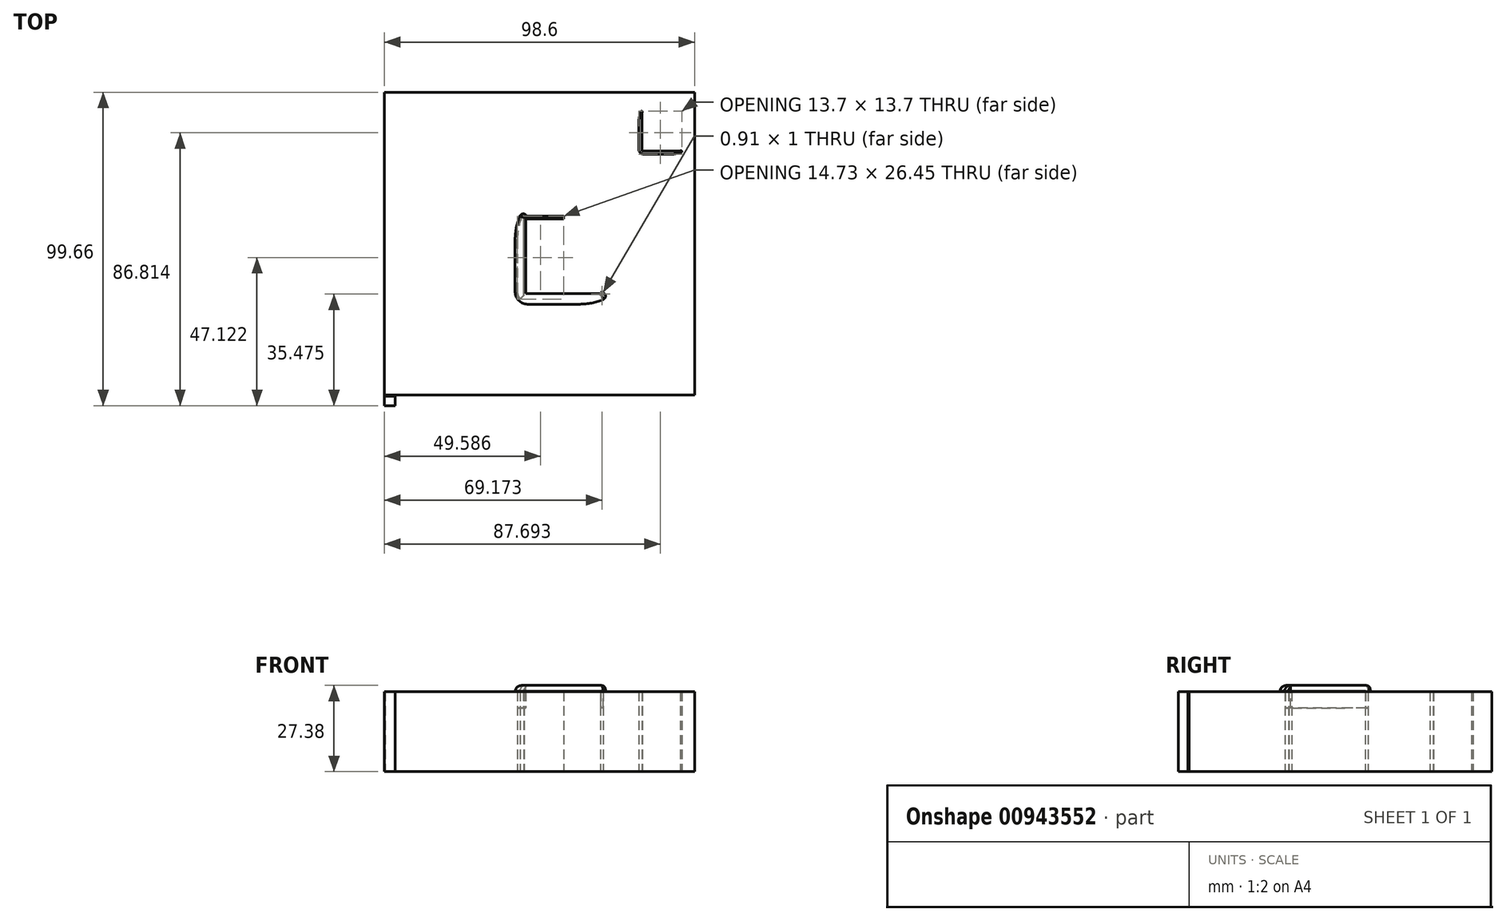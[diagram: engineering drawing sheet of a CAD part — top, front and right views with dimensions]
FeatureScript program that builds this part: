
annotation { "Feature Type Name" : "Feature", "Feature Type Description" : "" }
export const myFeature = defineFeature(function(context is Context, id is Id, definition is map)
    precondition{}
    {
        {
            var Q0;
            Q0=qCreatedBy(makeId("Top.planeOp"),FACE);
            var sketch = newSketch(context, id + "F0", { "sketchPlane" : qUnion([Q0])});
            skLineSegment(sketch, "E0", {"start": v(-49.3, -64.38) * mm, "end": v(49.3, -64.38) * mm});
            skLineSegment(sketch, "E1", {"start": v(49.3, -64.38) * mm, "end": v(49.3, 64.38) * mm});
            skLineSegment(sketch, "E2", {"start": v(49.3, 64.38) * mm, "end": v(-49.3, 64.38) * mm});
            skLineSegment(sketch, "E3", {"start": v(-49.3, 64.38) * mm, "end": v(-49.3, -64.38) * mm});
            skLineSegment(sketch, "E4", {"start": v(-49.3, 60.15) * mm, "end": v(49.3, 60.15) * mm});
            skLineSegment(sketch, "E5", {"start": v(49.3, 60.15) * mm, "end": v(49.3, 59.97) * mm});
            skLineSegment(sketch, "E6", {"start": v(49.3, 59.97) * mm, "end": v(-49.3, 59.97) * mm});
            skLineSegment(sketch, "E7", {"start": v(-49.3, 59.97) * mm, "end": v(-49.3, 60.15) * mm});
            skLineSegment(sketch, "E8", {"start": v(15.26, 64.38) * mm, "end": v(15.43, 64.38) * mm});
            skLineSegment(sketch, "E9", {"start": v(15.43, 64.38) * mm, "end": v(15.43, 59.97) * mm});
            skLineSegment(sketch, "E10", {"start": v(15.43, 59.97) * mm, "end": v(15.26, 59.97) * mm});
            skLineSegment(sketch, "E11", {"start": v(15.26, 59.97) * mm, "end": v(15.26, 64.38) * mm});
            skLineSegment(sketch, "E12", {"start": v(-49.12, -36.34) * mm, "end": v(49.3, -36.34) * mm});
            skLineSegment(sketch, "E13", {"start": v(49.3, -36.34) * mm, "end": v(49.3, -36.69) * mm});
            skLineSegment(sketch, "E14", {"start": v(49.3, -36.69) * mm, "end": v(-49.12, -36.69) * mm});
            skLineSegment(sketch, "E15", {"start": v(-49.12, -36.69) * mm, "end": v(-49.12, -36.34) * mm});
            skLineSegment(sketch, "E16", {"start": v(-6.44, -36.51) * mm, "end": v(-6.09, -36.51) * mm});
            skLineSegment(sketch, "E17", {"start": v(-6.09, -36.51) * mm, "end": v(-6.09, -64.2) * mm});
            skLineSegment(sketch, "E18", {"start": v(-6.09, -64.2) * mm, "end": v(-6.44, -64.2) * mm});
            skLineSegment(sketch, "E19", {"start": v(-6.44, -64.2) * mm, "end": v(-6.44, -36.51) * mm});
            skLineSegment(sketch, "E20", {"start": v(-6.44, -45.33) * mm, "end": v(49.12, -45.33) * mm});
            skLineSegment(sketch, "E21", {"start": v(49.12, -45.33) * mm, "end": v(49.12, -45.68) * mm});
            skLineSegment(sketch, "E22", {"start": v(49.12, -45.68) * mm, "end": v(-6.44, -45.68) * mm});
            skLineSegment(sketch, "E23", {"start": v(-6.44, -45.68) * mm, "end": v(-6.44, -45.33) * mm});
            skLineSegment(sketch, "E24", {"start": v(-6.44, -49.04) * mm, "end": v(49.12, -49.04) * mm});
            skLineSegment(sketch, "E25", {"start": v(49.12, -49.04) * mm, "end": v(49.12, -49.39) * mm});
            skLineSegment(sketch, "E26", {"start": v(49.12, -49.39) * mm, "end": v(-6.44, -49.39) * mm});
            skLineSegment(sketch, "E27", {"start": v(-6.44, -49.39) * mm, "end": v(-6.44, -49.04) * mm});
            skLineSegment(sketch, "E28", {"start": v(-6.09, -52.92) * mm, "end": v(49.3, -52.92) * mm});
            skLineSegment(sketch, "E29", {"start": v(49.3, -52.92) * mm, "end": v(49.3, -53.1) * mm});
            skLineSegment(sketch, "E30", {"start": v(49.3, -53.1) * mm, "end": v(-6.09, -53.1) * mm});
            skLineSegment(sketch, "E31", {"start": v(-6.09, -53.1) * mm, "end": v(-6.09, -52.92) * mm});
            skLineSegment(sketch, "E32", {"start": v(-6.09, -56.62) * mm, "end": v(49.3, -56.62) * mm});
            skLineSegment(sketch, "E33", {"start": v(49.3, -56.62) * mm, "end": v(49.3, -56.8) * mm});
            skLineSegment(sketch, "E34", {"start": v(49.3, -56.8) * mm, "end": v(-6.09, -56.8) * mm});
            skLineSegment(sketch, "E35", {"start": v(-6.09, -56.8) * mm, "end": v(-6.09, -56.62) * mm});
            skLineSegment(sketch, "E36", {"start": v(-6.09, -60.32) * mm, "end": v(49.3, -60.32) * mm});
            skLineSegment(sketch, "E37", {"start": v(49.3, -60.32) * mm, "end": v(49.3, -60.5) * mm});
            skLineSegment(sketch, "E38", {"start": v(49.3, -60.5) * mm, "end": v(-6.09, -60.5) * mm});
            skLineSegment(sketch, "E39", {"start": v(-6.09, -60.5) * mm, "end": v(-6.09, -60.32) * mm});
            skLineSegment(sketch, "E40", {"start": v(21.25, -49.04) * mm, "end": v(21.6, -49.04) * mm});
            skLineSegment(sketch, "E41", {"start": v(21.6, -49.04) * mm, "end": v(21.6, -64.2) * mm});
            skLineSegment(sketch, "E42", {"start": v(21.6, -64.2) * mm, "end": v(21.25, -64.2) * mm});
            skLineSegment(sketch, "E43", {"start": v(21.25, -64.2) * mm, "end": v(21.25, -49.04) * mm});
            skLineSegment(sketch, "E44", {"start": v(-49.3, -47.8) * mm, "end": v(-6.09, -47.8) * mm});
            skLineSegment(sketch, "E45", {"start": v(-6.09, -47.8) * mm, "end": v(-6.09, -48.15) * mm});
            skLineSegment(sketch, "E46", {"start": v(-6.09, -48.15) * mm, "end": v(-49.3, -48.15) * mm});
            skLineSegment(sketch, "E47", {"start": v(-49.3, -48.15) * mm, "end": v(-49.3, -47.8) * mm});
            skLineSegment(sketch, "E48", {"start": v(-49.3, -53.8) * mm, "end": v(-6.09, -53.8) * mm});
            skLineSegment(sketch, "E49", {"start": v(-6.09, -53.8) * mm, "end": v(-6.09, -50.98) * mm});
            skLineSegment(sketch, "E50", {"start": v(-6.09, -50.98) * mm, "end": v(-49.3, -50.98) * mm});
            skLineSegment(sketch, "E51", {"start": v(-49.3, -50.98) * mm, "end": v(-49.3, -53.8) * mm});
            skLineSegment(sketch, "E52", {"start": v(-49.3, -59.09) * mm, "end": v(-6.09, -59.09) * mm});
            skLineSegment(sketch, "E53", {"start": v(-6.09, -59.09) * mm, "end": v(-6.09, -56.27) * mm});
            skLineSegment(sketch, "E54", {"start": v(-6.09, -56.27) * mm, "end": v(-49.3, -56.27) * mm});
            skLineSegment(sketch, "E55", {"start": v(-49.3, -56.27) * mm, "end": v(-49.3, -59.09) * mm});
            skLineSegment(sketch, "E56", {"start": v(-49.3, -64.38) * mm, "end": v(-6.09, -64.38) * mm});
            skLineSegment(sketch, "E57", {"start": v(-6.09, -64.38) * mm, "end": v(-6.09, -61.56) * mm});
            skLineSegment(sketch, "E58", {"start": v(-6.09, -61.56) * mm, "end": v(-49.3, -61.56) * mm});
            skLineSegment(sketch, "E59", {"start": v(-49.3, -61.56) * mm, "end": v(-49.3, -64.38) * mm});
            skLineSegment(sketch, "E60", {"start": v(-49.3, -48.15) * mm, "end": v(-6.09, -48.15) * mm});
            skLineSegment(sketch, "E61", {"start": v(-6.09, -48.15) * mm, "end": v(-6.09, -45.33) * mm});
            skLineSegment(sketch, "E62", {"start": v(-6.09, -45.33) * mm, "end": v(-49.3, -45.33) * mm});
            skLineSegment(sketch, "E63", {"start": v(-49.3, -45.33) * mm, "end": v(-49.3, -48.15) * mm});
            skLineSegment(sketch, "E64", {"start": v(-49.3, -42.5) * mm, "end": v(-6.09, -42.5) * mm});
            skLineSegment(sketch, "E65", {"start": v(-6.09, -42.5) * mm, "end": v(-6.09, -39.69) * mm});
            skLineSegment(sketch, "E66", {"start": v(-6.09, -39.69) * mm, "end": v(-49.3, -39.69) * mm});
            skLineSegment(sketch, "E67", {"start": v(-49.3, -39.69) * mm, "end": v(-49.3, -42.5) * mm});
            skArc(sketch, "E68", {"start": v(-46.48, -62.8) * mm, "mid": v(-46.5, -62.62) * mm, "end": v(-46.54, -62.46) * mm});
            skArc(sketch, "E69", {"start": v(-46.54, -62.46) * mm, "mid": v(-46.63, -62.3) * mm, "end": v(-46.74, -62.17) * mm});
            skArc(sketch, "E70", {"start": v(-46.74, -62.17) * mm, "mid": v(-46.87, -62.06) * mm, "end": v(-47.02, -61.98) * mm});
            skArc(sketch, "E71", {"start": v(-47.02, -61.98) * mm, "mid": v(-47.19, -61.93) * mm, "end": v(-47.36, -61.91) * mm});
            skArc(sketch, "E72", {"start": v(-47.36, -61.91) * mm, "mid": v(-47.53, -61.93) * mm, "end": v(-47.7, -61.98) * mm});
            skArc(sketch, "E73", {"start": v(-47.7, -61.98) * mm, "mid": v(-47.85, -62.06) * mm, "end": v(-47.98, -62.17) * mm});
            skArc(sketch, "E74", {"start": v(-47.98, -62.17) * mm, "mid": v(-48.1, -62.3) * mm, "end": v(-48.17, -62.46) * mm});
            skArc(sketch, "E75", {"start": v(-48.17, -62.46) * mm, "mid": v(-48.22, -62.62) * mm, "end": v(-48.24, -62.8) * mm});
            skArc(sketch, "E76", {"start": v(-48.24, -62.8) * mm, "mid": v(-48.22, -62.97) * mm, "end": v(-48.17, -63.13) * mm});
            skArc(sketch, "E77", {"start": v(-48.17, -63.13) * mm, "mid": v(-48.1, -63.28) * mm, "end": v(-47.98, -63.42) * mm});
            skArc(sketch, "E78", {"start": v(-47.98, -63.42) * mm, "mid": v(-47.85, -63.53) * mm, "end": v(-47.7, -63.6) * mm});
            skArc(sketch, "E79", {"start": v(-47.7, -63.6) * mm, "mid": v(-47.53, -63.66) * mm, "end": v(-47.36, -63.68) * mm});
            skArc(sketch, "E80", {"start": v(-47.36, -63.68) * mm, "mid": v(-47.19, -63.66) * mm, "end": v(-47.02, -63.6) * mm});
            skArc(sketch, "E81", {"start": v(-47.02, -63.6) * mm, "mid": v(-46.87, -63.53) * mm, "end": v(-46.74, -63.42) * mm});
            skArc(sketch, "E82", {"start": v(-46.74, -63.42) * mm, "mid": v(-46.63, -63.28) * mm, "end": v(-46.54, -63.13) * mm});
            skArc(sketch, "E83", {"start": v(-46.54, -63.13) * mm, "mid": v(-46.5, -62.97) * mm, "end": v(-46.48, -62.8) * mm});
            skArc(sketch, "E84", {"start": v(-38.01, -62.8) * mm, "mid": v(-38.03, -62.62) * mm, "end": v(-38.08, -62.46) * mm});
            skArc(sketch, "E85", {"start": v(-38.08, -62.46) * mm, "mid": v(-38.16, -62.3) * mm, "end": v(-38.27, -62.17) * mm});
            skArc(sketch, "E86", {"start": v(-38.27, -62.17) * mm, "mid": v(-38.4, -62.06) * mm, "end": v(-38.56, -61.98) * mm});
            skArc(sketch, "E87", {"start": v(-38.56, -61.98) * mm, "mid": v(-38.72, -61.93) * mm, "end": v(-38.9, -61.91) * mm});
            skArc(sketch, "E88", {"start": v(-38.9, -61.91) * mm, "mid": v(-39.07, -61.93) * mm, "end": v(-39.23, -61.98) * mm});
            skArc(sketch, "E89", {"start": v(-39.23, -61.98) * mm, "mid": v(-39.38, -62.06) * mm, "end": v(-39.52, -62.17) * mm});
            skArc(sketch, "E90", {"start": v(-39.52, -62.17) * mm, "mid": v(-39.63, -62.3) * mm, "end": v(-39.7, -62.46) * mm});
            skArc(sketch, "E91", {"start": v(-39.7, -62.46) * mm, "mid": v(-39.76, -62.62) * mm, "end": v(-39.78, -62.8) * mm});
            skArc(sketch, "E92", {"start": v(-39.78, -62.8) * mm, "mid": v(-39.76, -62.97) * mm, "end": v(-39.7, -63.13) * mm});
            skArc(sketch, "E93", {"start": v(-39.7, -63.13) * mm, "mid": v(-39.63, -63.28) * mm, "end": v(-39.52, -63.42) * mm});
            skArc(sketch, "E94", {"start": v(-39.52, -63.42) * mm, "mid": v(-39.38, -63.53) * mm, "end": v(-39.23, -63.6) * mm});
            skArc(sketch, "E95", {"start": v(-39.23, -63.6) * mm, "mid": v(-39.07, -63.66) * mm, "end": v(-38.9, -63.68) * mm});
            skArc(sketch, "E96", {"start": v(-38.9, -63.68) * mm, "mid": v(-38.72, -63.66) * mm, "end": v(-38.56, -63.6) * mm});
            skArc(sketch, "E97", {"start": v(-38.56, -63.6) * mm, "mid": v(-38.4, -63.53) * mm, "end": v(-38.27, -63.42) * mm});
            skArc(sketch, "E98", {"start": v(-38.27, -63.42) * mm, "mid": v(-38.16, -63.28) * mm, "end": v(-38.08, -63.13) * mm});
            skArc(sketch, "E99", {"start": v(-38.08, -63.13) * mm, "mid": v(-38.03, -62.97) * mm, "end": v(-38.01, -62.8) * mm});
            skArc(sketch, "E100", {"start": v(-23.55, -62.8) * mm, "mid": v(-23.56, -62.62) * mm, "end": v(-23.62, -62.46) * mm});
            skArc(sketch, "E101", {"start": v(-23.62, -62.46) * mm, "mid": v(-23.7, -62.3) * mm, "end": v(-23.8, -62.17) * mm});
            skArc(sketch, "E102", {"start": v(-23.8, -62.17) * mm, "mid": v(-23.94, -62.06) * mm, "end": v(-24.1, -61.98) * mm});
            skArc(sketch, "E103", {"start": v(-24.1, -61.98) * mm, "mid": v(-24.26, -61.93) * mm, "end": v(-24.43, -61.91) * mm});
            skArc(sketch, "E104", {"start": v(-24.43, -61.91) * mm, "mid": v(-24.6, -61.93) * mm, "end": v(-24.77, -61.98) * mm});
            skArc(sketch, "E105", {"start": v(-24.77, -61.98) * mm, "mid": v(-24.92, -62.06) * mm, "end": v(-25.05, -62.17) * mm});
            skArc(sketch, "E106", {"start": v(-25.05, -62.17) * mm, "mid": v(-25.16, -62.3) * mm, "end": v(-25.24, -62.46) * mm});
            skArc(sketch, "E107", {"start": v(-25.24, -62.46) * mm, "mid": v(-25.3, -62.62) * mm, "end": v(-25.31, -62.8) * mm});
            skArc(sketch, "E108", {"start": v(-25.31, -62.8) * mm, "mid": v(-25.3, -62.97) * mm, "end": v(-25.24, -63.13) * mm});
            skArc(sketch, "E109", {"start": v(-25.24, -63.13) * mm, "mid": v(-25.16, -63.28) * mm, "end": v(-25.05, -63.42) * mm});
            skArc(sketch, "E110", {"start": v(-25.05, -63.42) * mm, "mid": v(-24.92, -63.53) * mm, "end": v(-24.77, -63.6) * mm});
            skArc(sketch, "E111", {"start": v(-24.77, -63.6) * mm, "mid": v(-24.6, -63.66) * mm, "end": v(-24.43, -63.68) * mm});
            skArc(sketch, "E112", {"start": v(-24.43, -63.68) * mm, "mid": v(-24.26, -63.66) * mm, "end": v(-24.1, -63.6) * mm});
            skArc(sketch, "E113", {"start": v(-24.1, -63.6) * mm, "mid": v(-23.94, -63.53) * mm, "end": v(-23.8, -63.42) * mm});
            skArc(sketch, "E114", {"start": v(-23.8, -63.42) * mm, "mid": v(-23.7, -63.28) * mm, "end": v(-23.62, -63.13) * mm});
            skArc(sketch, "E115", {"start": v(-23.62, -63.13) * mm, "mid": v(-23.56, -62.97) * mm, "end": v(-23.55, -62.8) * mm});
            skLineSegment(sketch, "E116", {"start": v(-4.68, -39.46) * mm, "end": v(-4.68, -39.2) * mm});
            skLineSegment(sketch, "E117", {"start": v(-4.68, -39.2) * mm, "end": v(-2.48, -39.2) * mm});
            skLineSegment(sketch, "E118", {"start": v(-2.48, -39.2) * mm, "end": v(-2.48, -38.95) * mm});
            skLineSegment(sketch, "E119", {"start": v(-2.48, -38.95) * mm, "end": v(-4.68, -38.95) * mm});
            skLineSegment(sketch, "E120", {"start": v(-4.68, -38.95) * mm, "end": v(-4.68, -37.29) * mm});
            skLineSegment(sketch, "E121", {"start": v(-4.68, -37.29) * mm, "end": v(-1.9, -37.29) * mm});
            skArc(sketch, "E122", {"start": v(-1.9, -37.3) * mm, "mid": v(-1.01, -37.67) * mm, "end": v(-0.64, -38.57) * mm});
            skArc(sketch, "E123", {"start": v(-0.64, -38.57) * mm, "mid": v(-1.01, -39.46) * mm, "end": v(-1.9, -39.84) * mm});
            skLineSegment(sketch, "E124", {"start": v(-1.9, -39.84) * mm, "end": v(-2.48, -39.84) * mm});
            skLineSegment(sketch, "E125", {"start": v(-2.48, -39.84) * mm, "end": v(-2.48, -39.97) * mm});
            skLineSegment(sketch, "E126", {"start": v(-2.48, -39.97) * mm, "end": v(-4.68, -39.97) * mm});
            skLineSegment(sketch, "E127", {"start": v(-4.68, -39.97) * mm, "end": v(-4.68, -39.72) * mm});
            skLineSegment(sketch, "E128", {"start": v(-4.68, -39.72) * mm, "end": v(-2.48, -39.72) * mm});
            skLineSegment(sketch, "E129", {"start": v(-2.48, -39.72) * mm, "end": v(-2.48, -39.46) * mm});
            skLineSegment(sketch, "E130", {"start": v(-2.48, -39.46) * mm, "end": v(-4.68, -39.46) * mm});
            skLineSegment(sketch, "E131", {"start": v(-2.48, -40.23) * mm, "end": v(-4.68, -40.23) * mm});
            skLineSegment(sketch, "E132", {"start": v(-2.48, -40.48) * mm, "end": v(-4.68, -40.48) * mm});
            skLineSegment(sketch, "E133", {"start": v(-4.68, -40.48) * mm, "end": v(-4.68, -40.23) * mm});
            skLineSegment(sketch, "E134", {"start": v(-2.48, -40.23) * mm, "end": v(-2.48, -40.48) * mm});
            skLineSegment(sketch, "E135", {"start": v(2.09, -38.5) * mm, "end": v(3.79, -39.27) * mm});
            skLineSegment(sketch, "E136", {"start": v(2.53, -39.59) * mm, "end": v(1.84, -39.59) * mm});
            skLineSegment(sketch, "E137", {"start": v(0.7, -37.29) * mm, "end": v(4.11, -37.29) * mm});
            skLineSegment(sketch, "E138", {"start": v(0.7, -37.29) * mm, "end": v(2.68, -38.18) * mm});
            skLineSegment(sketch, "E139", {"start": v(-0.28, -37.73) * mm, "end": v(3.13, -39.27) * mm});
            skLineSegment(sketch, "E140", {"start": v(2.09, -38.5) * mm, "end": v(2.74, -38.5) * mm});
            skLineSegment(sketch, "E141", {"start": v(4.11, -40.48) * mm, "end": v(-0.28, -40.48) * mm});
            skLineSegment(sketch, "E142", {"start": v(-0.28, -38.32) * mm, "end": v(-0.28, -40.48) * mm});
            skLineSegment(sketch, "E143", {"start": v(1.84, -39.27) * mm, "end": v(1.84, -39.59) * mm});
            skLineSegment(sketch, "E144", {"start": v(-0.28, -37.44) * mm, "end": v(1.84, -38.39) * mm});
            skLineSegment(sketch, "E145", {"start": v(0.05, -37.29) * mm, "end": v(2.03, -38.18) * mm});
            skLineSegment(sketch, "E146", {"start": v(-0.28, -37.73) * mm, "end": v(-0.28, -38.03) * mm});
            skLineSegment(sketch, "E147", {"start": v(-0.28, -37.29) * mm, "end": v(0.05, -37.29) * mm});
            skLineSegment(sketch, "E148", {"start": v(-0.28, -37.29) * mm, "end": v(-0.28, -37.44) * mm});
            skLineSegment(sketch, "E149", {"start": v(1.84, -38.18) * mm, "end": v(1.84, -38.39) * mm});
            skLineSegment(sketch, "E150", {"start": v(1.84, -38.18) * mm, "end": v(2.03, -38.18) * mm});
            skLineSegment(sketch, "E151", {"start": v(3.4, -38.5) * mm, "end": v(4.11, -38.83) * mm});
            skLineSegment(sketch, "E152", {"start": v(2.74, -38.5) * mm, "end": v(4.11, -39.12) * mm});
            skLineSegment(sketch, "E153", {"start": v(4.11, -38.5) * mm, "end": v(4.11, -38.83) * mm});
            skLineSegment(sketch, "E154", {"start": v(3.84, -39.59) * mm, "end": v(4.11, -39.71) * mm});
            skLineSegment(sketch, "E155", {"start": v(2.53, -39.59) * mm, "end": v(4.11, -40.3) * mm});
            skLineSegment(sketch, "E156", {"start": v(3.19, -39.59) * mm, "end": v(4.11, -40) * mm});
            skLineSegment(sketch, "E157", {"start": v(4.11, -39.27) * mm, "end": v(3.79, -39.27) * mm});
            skLineSegment(sketch, "E158", {"start": v(3.13, -39.27) * mm, "end": v(2.48, -39.27) * mm});
            skLineSegment(sketch, "E159", {"start": v(3.84, -39.59) * mm, "end": v(3.19, -39.59) * mm});
            skLineSegment(sketch, "E160", {"start": v(4.11, -40.3) * mm, "end": v(4.11, -40.48) * mm});
            skLineSegment(sketch, "E161", {"start": v(4.11, -39.12) * mm, "end": v(4.11, -39.27) * mm});
            skLineSegment(sketch, "E162", {"start": v(4.11, -39.71) * mm, "end": v(4.11, -40) * mm});
            skLineSegment(sketch, "E163", {"start": v(2.68, -38.18) * mm, "end": v(4.11, -38.18) * mm});
            skLineSegment(sketch, "E164", {"start": v(3.4, -38.5) * mm, "end": v(4.11, -38.5) * mm});
            skLineSegment(sketch, "E165", {"start": v(4.11, -37.29) * mm, "end": v(4.11, -38.18) * mm});
            skLineSegment(sketch, "E166", {"start": v(-0.28, -38.32) * mm, "end": v(-0.28, -38.03) * mm});
            skLineSegment(sketch, "E167", {"start": v(1.84, -39.27) * mm, "end": v(2.48, -39.27) * mm});
            skLineSegment(sketch, "E168", {"start": v(-49.12, -36.34) * mm, "end": v(-45.95, -36.34) * mm});
            skLineSegment(sketch, "E169", {"start": v(-45.95, -36.34) * mm, "end": v(-45.95, -47.8) * mm});
            skLineSegment(sketch, "E170", {"start": v(-2.58, -40.48) * mm, "end": v(-2.48, -40.43) * mm});
            skLineSegment(sketch, "E171", {"start": v(1.97, -37.86) * mm, "end": v(2.95, -37.29) * mm});
            skLineSegment(sketch, "E172", {"start": v(-1.32, -39.76) * mm, "end": v(-0.63, -39.36) * mm});
            skLineSegment(sketch, "E173", {"start": v(1.4, -38.2) * mm, "end": v(1.68, -38.03) * mm});
            skLineSegment(sketch, "E174", {"start": v(-0.28, -39.16) * mm, "end": v(1.1, -38.36) * mm});
            skLineSegment(sketch, "E175", {"start": v(-3.21, -40.48) * mm, "end": v(-2.77, -40.23) * mm});
            skLineSegment(sketch, "E176", {"start": v(1.6, -37.7) * mm, "end": v(2.32, -37.29) * mm});
            skLineSegment(sketch, "E177", {"start": v(-2.1, -39.84) * mm, "end": v(-0.31, -38.8) * mm});
            skLineSegment(sketch, "E178", {"start": v(1.04, -38.03) * mm, "end": v(1.32, -37.86) * mm});
            skLineSegment(sketch, "E179", {"start": v(-0.28, -38.8) * mm, "end": v(0.75, -38.2) * mm});
            skLineSegment(sketch, "E180", {"start": v(-3.85, -40.48) * mm, "end": v(-3.4, -40.23) * mm});
            skLineSegment(sketch, "E181", {"start": v(1.25, -37.54) * mm, "end": v(1.68, -37.29) * mm});
            skLineSegment(sketch, "E182", {"start": v(-2.96, -39.97) * mm, "end": v(-2.52, -39.72) * mm});
            skLineSegment(sketch, "E183", {"start": v(0.68, -37.87) * mm, "end": v(0.97, -37.7) * mm});
            skLineSegment(sketch, "E184", {"start": v(-2.48, -39.7) * mm, "end": v(-0.3, -38.43) * mm});
            skLineSegment(sketch, "E185", {"start": v(-0.28, -38.42) * mm, "end": v(0.4, -38.03) * mm});
            skLineSegment(sketch, "E186", {"start": v(-4.48, -40.48) * mm, "end": v(-4.04, -40.23) * mm});
            skLineSegment(sketch, "E187", {"start": v(0.9, -37.38) * mm, "end": v(1.05, -37.29) * mm});
            skLineSegment(sketch, "E188", {"start": v(-3.6, -39.97) * mm, "end": v(-3.15, -39.72) * mm});
            skLineSegment(sketch, "E189", {"start": v(0.32, -37.7) * mm, "end": v(0.6, -37.54) * mm});
            skLineSegment(sketch, "E190", {"start": v(-2.71, -39.46) * mm, "end": v(-0.39, -38.12) * mm});
            skLineSegment(sketch, "E191", {"start": v(-0.28, -38.06) * mm, "end": v(0.04, -37.87) * mm});
            skLineSegment(sketch, "E192", {"start": v(-4.68, -40.23) * mm, "end": v(-4.67, -40.23) * mm});
            skLineSegment(sketch, "E193", {"start": v(-0.03, -37.55) * mm, "end": v(0.25, -37.38) * mm});
            skLineSegment(sketch, "E194", {"start": v(-4.23, -39.97) * mm, "end": v(-3.79, -39.72) * mm});
            skLineSegment(sketch, "E195", {"start": v(-2.48, -38.96) * mm, "end": v(-0.56, -37.85) * mm});
            skLineSegment(sketch, "E196", {"start": v(-3.35, -39.46) * mm, "end": v(-2.9, -39.2) * mm});
            skLineSegment(sketch, "E197", {"start": v(-4.68, -39.86) * mm, "end": v(-4.42, -39.72) * mm});
            skLineSegment(sketch, "E198", {"start": v(-0.28, -37.32) * mm, "end": v(-0.22, -37.29) * mm});
            skLineSegment(sketch, "E199", {"start": v(-3.98, -39.46) * mm, "end": v(-3.54, -39.2) * mm});
            skLineSegment(sketch, "E200", {"start": v(-3.1, -38.95) * mm, "end": v(-0.8, -37.63) * mm});
            skLineSegment(sketch, "E201", {"start": v(-4.62, -39.46) * mm, "end": v(-4.18, -39.2) * mm});
            skLineSegment(sketch, "E202", {"start": v(-3.73, -38.95) * mm, "end": v(-1.13, -37.45) * mm});
            skLineSegment(sketch, "E203", {"start": v(-4.37, -38.95) * mm, "end": v(-1.55, -37.32) * mm});
            skLineSegment(sketch, "E204", {"start": v(-4.68, -38.76) * mm, "end": v(-2.13, -37.29) * mm});
            skLineSegment(sketch, "E205", {"start": v(-4.68, -38.4) * mm, "end": v(-2.76, -37.29) * mm});
            skLineSegment(sketch, "E206", {"start": v(-4.68, -38.03) * mm, "end": v(-3.4, -37.29) * mm});
            skLineSegment(sketch, "E207", {"start": v(-4.68, -37.66) * mm, "end": v(-4.03, -37.29) * mm});
            skLineSegment(sketch, "E208", {"start": v(-4.68, -37.3) * mm, "end": v(-4.67, -37.29) * mm});
            skLineSegment(sketch, "E209", {"start": v(-0.28, -39.52) * mm, "end": v(1.46, -38.52) * mm});
            skLineSegment(sketch, "E210", {"start": v(2.32, -38.02) * mm, "end": v(3.59, -37.29) * mm});
            skLineSegment(sketch, "E211", {"start": v(1.75, -38.35) * mm, "end": v(1.84, -38.3) * mm});
            skLineSegment(sketch, "E212", {"start": v(-0.28, -39.9) * mm, "end": v(1.82, -38.68) * mm});
            skLineSegment(sketch, "E213", {"start": v(2.68, -38.18) * mm, "end": v(4.11, -37.35) * mm});
            skLineSegment(sketch, "E214", {"start": v(2.1, -38.51) * mm, "end": v(2.12, -38.5) * mm});
            skLineSegment(sketch, "E215", {"start": v(-0.28, -40.26) * mm, "end": v(2.18, -38.84) * mm});
            skLineSegment(sketch, "E216", {"start": v(3.3, -38.18) * mm, "end": v(4.11, -37.72) * mm});
            skLineSegment(sketch, "E217", {"start": v(2.46, -38.67) * mm, "end": v(2.75, -38.5) * mm});
            skLineSegment(sketch, "E218", {"start": v(-0.04, -40.48) * mm, "end": v(1.84, -39.4) * mm});
            skLineSegment(sketch, "E219", {"start": v(3.94, -38.18) * mm, "end": v(4.11, -38.09) * mm});
            skLineSegment(sketch, "E220", {"start": v(2.06, -39.27) * mm, "end": v(2.53, -39) * mm});
            skLineSegment(sketch, "E221", {"start": v(2.82, -38.83) * mm, "end": v(3.1, -38.67) * mm});
            skLineSegment(sketch, "E222", {"start": v(0.6, -40.48) * mm, "end": v(2.15, -39.59) * mm});
            skLineSegment(sketch, "E223", {"start": v(3.75, -38.66) * mm, "end": v(4.03, -38.5) * mm});
            skLineSegment(sketch, "E224", {"start": v(2.7, -39.27) * mm, "end": v(2.89, -39.16) * mm});
            skLineSegment(sketch, "E225", {"start": v(3.18, -39) * mm, "end": v(3.46, -38.83) * mm});
            skLineSegment(sketch, "E226", {"start": v(1.23, -40.48) * mm, "end": v(2.67, -39.65) * mm});
            skLineSegment(sketch, "E227", {"start": v(4.1, -38.82) * mm, "end": v(4.11, -38.82) * mm});
            skLineSegment(sketch, "E228", {"start": v(3.53, -39.15) * mm, "end": v(3.82, -38.99) * mm});
            skLineSegment(sketch, "E229", {"start": v(1.87, -40.48) * mm, "end": v(3.03, -39.81) * mm});
            skLineSegment(sketch, "E230", {"start": v(3.97, -39.27) * mm, "end": v(4.11, -39.19) * mm});
            skLineSegment(sketch, "E231", {"start": v(3.32, -39.65) * mm, "end": v(3.42, -39.59) * mm});
            skLineSegment(sketch, "E232", {"start": v(2.5, -40.48) * mm, "end": v(3.39, -39.97) * mm});
            skLineSegment(sketch, "E233", {"start": v(3.67, -39.8) * mm, "end": v(3.96, -39.64) * mm});
            skLineSegment(sketch, "E234", {"start": v(3.14, -40.48) * mm, "end": v(3.74, -40.13) * mm});
            skLineSegment(sketch, "E235", {"start": v(4.03, -39.97) * mm, "end": v(4.11, -39.92) * mm});
            skLineSegment(sketch, "E236", {"start": v(3.77, -40.48) * mm, "end": v(4.1, -40.3) * mm});
            skLineSegment(sketch, "E237", {"start": v(6.9, 7.22) * mm, "end": v(-11.38, -11.05) * mm});
            skLineSegment(sketch, "E238", {"start": v(44.8, 41.29) * mm, "end": v(32.79, 41.29) * mm});
            skArc(sketch, "E239", {"start": v(32.79, 41.29) * mm, "mid": v(32.7, 41.3) * mm, "end": v(32.62, 41.36) * mm});
            skArc(sketch, "E240", {"start": v(32.62, 41.36) * mm, "mid": v(32.57, 41.43) * mm, "end": v(32.56, 41.52) * mm});
            skLineSegment(sketch, "E241", {"start": v(32.56, 41.52) * mm, "end": v(32.56, 53.52) * mm});
            skArc(sketch, "E242", {"start": v(32.56, 53.52) * mm, "mid": v(32.75, 53.77) * mm, "end": v(32.52, 53.98) * mm});
            skLineSegment(sketch, "E243", {"start": v(32.52, 53.98) * mm, "end": v(32.46, 53.98) * mm});
            skArc(sketch, "E244", {"start": v(32.46, 53.98) * mm, "mid": v(32.33, 53.94) * mm, "end": v(32.24, 53.83) * mm});
            skArc(sketch, "E245", {"start": v(32.24, 53.83) * mm, "mid": v(31.72, 52.07) * mm, "end": v(31.54, 50.24) * mm});
            skLineSegment(sketch, "E246", {"start": v(31.54, 50.24) * mm, "end": v(31.54, 41.9) * mm});
            skArc(sketch, "E247", {"start": v(31.54, 41.9) * mm, "mid": v(31.67, 41.28) * mm, "end": v(32.02, 40.75) * mm});
            skArc(sketch, "E248", {"start": v(32.02, 40.75) * mm, "mid": v(32.55, 40.4) * mm, "end": v(33.17, 40.27) * mm});
            skLineSegment(sketch, "E249", {"start": v(33.17, 40.27) * mm, "end": v(41.51, 40.27) * mm});
            skArc(sketch, "E250", {"start": v(41.51, 40.27) * mm, "mid": v(43.34, 40.45) * mm, "end": v(45.1, 40.98) * mm});
            skArc(sketch, "E251", {"start": v(45.1, 40.98) * mm, "mid": v(45.2, 41.06) * mm, "end": v(45.24, 41.19) * mm});
            skLineSegment(sketch, "E252", {"start": v(45.24, 41.19) * mm, "end": v(45.24, 41.25) * mm});
            skArc(sketch, "E253", {"start": v(45.24, 41.25) * mm, "mid": v(45.03, 41.48) * mm, "end": v(44.8, 41.29) * mm});
            skLineSegment(sketch, "E254", {"start": v(19.42, -4.72) * mm, "end": v(-4.6, -4.72) * mm});
            skArc(sketch, "E255", {"start": v(-4.6, -4.72) * mm, "mid": v(-4.77, -4.68) * mm, "end": v(-4.91, -4.58) * mm});
            skArc(sketch, "E256", {"start": v(-4.91, -4.58) * mm, "mid": v(-5.01, -4.43) * mm, "end": v(-5.05, -4.26) * mm});
            skLineSegment(sketch, "E257", {"start": v(-5.05, -4.26) * mm, "end": v(-5.05, 19.75) * mm});
            skArc(sketch, "E258", {"start": v(-5.05, 19.75) * mm, "mid": v(-4.67, 20.24) * mm, "end": v(-5.12, 20.66) * mm});
            skLineSegment(sketch, "E259", {"start": v(-5.12, 20.66) * mm, "end": v(-5.25, 20.66) * mm});
            skArc(sketch, "E260", {"start": v(-5.25, 20.66) * mm, "mid": v(-5.5, 20.58) * mm, "end": v(-5.67, 20.37) * mm});
            skArc(sketch, "E261", {"start": v(-5.67, 20.37) * mm, "mid": v(-6.73, 16.85) * mm, "end": v(-7.08, 13.2) * mm});
            skLineSegment(sketch, "E262", {"start": v(-7.08, 13.2) * mm, "end": v(-7.08, -3.49) * mm});
            skArc(sketch, "E263", {"start": v(-7.08, -3.49) * mm, "mid": v(-6.83, -4.74) * mm, "end": v(-6.13, -5.8) * mm});
            skArc(sketch, "E264", {"start": v(-6.13, -5.8) * mm, "mid": v(-5.07, -6.5) * mm, "end": v(-3.82, -6.75) * mm});
            skLineSegment(sketch, "E265", {"start": v(-3.82, -6.75) * mm, "end": v(12.86, -6.75) * mm});
            skArc(sketch, "E266", {"start": v(12.86, -6.75) * mm, "mid": v(16.52, -6.4) * mm, "end": v(20.04, -5.34) * mm});
            skArc(sketch, "E267", {"start": v(20.04, -5.34) * mm, "mid": v(20.25, -5.17) * mm, "end": v(20.33, -4.92) * mm});
            skLineSegment(sketch, "E268", {"start": v(20.33, -4.92) * mm, "end": v(20.33, -4.8) * mm});
            skArc(sketch, "E269", {"start": v(20.33, -4.8) * mm, "mid": v(19.9, -4.34) * mm, "end": v(19.42, -4.72) * mm});
            skSolve(sketch);
        }
        {
            var Q0;
            Q0=makeQuery(id+"F0.imprint","IMPRINT",FACE,{"disambiguationData":[TD([[makeQuery(id+"F0.imprint","IMPRINT",EDGE,{"derivedFrom":sQuery(id+"F0.wireOp",EDGE,"E254")}),1.0]])]});
            var Q1;
            {var subQ0=sQuery(id+"F0.wireOp",EDGE,"E256");Q1=makeQuery(id+"F0.imprint","IMPRINT",FACE,{"disambiguationData":[TD([[makeQuery(id+"F0.imprint","IMPRINT",EDGE,{"derivedFrom":subQ0}),1.0]])]});}
            extrude(context, id + "F1", {"entities" : qUnion([Q0, Q1]), "depth" : 25.4 * mm});
        }
        {
            var Q0;
            Q0=makeQuery(id+"F1.opExtrude","CAP_FACE",FACE,{"disambiguationData":[OSD([sQuery(id+"F0.wireOp",EDGE,"E254"),sQuery(id+"F0.wireOp",EDGE,"E255"),sQuery(id+"F0.wireOp",EDGE,"E256"),sQuery(id+"F0.wireOp",EDGE,"E257"),sQuery(id+"F0.wireOp",EDGE,"E258"),sQuery(id+"F0.wireOp",EDGE,"E259"),sQuery(id+"F0.wireOp",EDGE,"E260"),sQuery(id+"F0.wireOp",EDGE,"E261"),sQuery(id+"F0.wireOp",EDGE,"E262"),sQuery(id+"F0.wireOp",EDGE,"E263"),sQuery(id+"F0.wireOp",EDGE,"E264"),sQuery(id+"F0.wireOp",EDGE,"E265"),sQuery(id+"F0.wireOp",EDGE,"E266"),sQuery(id+"F0.wireOp",EDGE,"E267"),sQuery(id+"F0.wireOp",EDGE,"E268"),sQuery(id+"F0.wireOp",EDGE,"E269")])],"isStart":true});
            var sketch = newSketch(context, id + "F2", { "sketchPlane" : qUnion([Q0])});
            skLineSegment(sketch, "E270.bottom", {"start": v(19.42, 4.72) * mm, "end": v(20.33, 4.72) * mm});
            skLineSegment(sketch, "E270.top", {"start": v(19.42, 3.71) * mm, "end": v(20.33, 3.71) * mm});
            skLineSegment(sketch, "E270.left", {"start": v(19.42, 4.72) * mm, "end": v(19.42, 3.71) * mm});
            skLineSegment(sketch, "E270.right", {"start": v(20.33, 4.72) * mm, "end": v(20.33, 3.71) * mm});
            skSolve(sketch);
        }
        {
            var Q0;
            Q0=qSketchRegion(id+"F2",true);
            extrude(context, id + "F3", {"entities" : qUnion([Q0]), "operationType" : NewBodyOperationType.REMOVE, "endBound" : BoundingType.THROUGH_ALL, "oppositeDirection" : true, "depth" : 25.4 * mm});
        }
        {
            var Q0;
            Q0=makeQuery(id+"F1.opExtrude","CAP_FACE",FACE,{"disambiguationData":[OSD([sQuery(id+"F0.wireOp",EDGE,"E254"),sQuery(id+"F0.wireOp",EDGE,"E255"),sQuery(id+"F0.wireOp",EDGE,"E256"),sQuery(id+"F0.wireOp",EDGE,"E257"),sQuery(id+"F0.wireOp",EDGE,"E258"),sQuery(id+"F0.wireOp",EDGE,"E259"),sQuery(id+"F0.wireOp",EDGE,"E260"),sQuery(id+"F0.wireOp",EDGE,"E261"),sQuery(id+"F0.wireOp",EDGE,"E262"),sQuery(id+"F0.wireOp",EDGE,"E263"),sQuery(id+"F0.wireOp",EDGE,"E264"),sQuery(id+"F0.wireOp",EDGE,"E265"),sQuery(id+"F0.wireOp",EDGE,"E266"),sQuery(id+"F0.wireOp",EDGE,"E267"),sQuery(id+"F0.wireOp",EDGE,"E268"),sQuery(id+"F0.wireOp",EDGE,"E269")])],"isStart":true});
            var sketch = newSketch(context, id + "F4", { "sketchPlane" : qUnion([Q0])});
            skLineSegment(sketch, "E271.bottom", {"start": v(7.65, -20.65) * mm, "end": v(-5.05, -20.65) * mm});
            skLineSegment(sketch, "E271.top", {"start": v(7.65, -19.75) * mm, "end": v(-5.05, -19.75) * mm});
            skLineSegment(sketch, "E271.left", {"start": v(7.65, -20.65) * mm, "end": v(7.65, -19.75) * mm});
            skLineSegment(sketch, "E271.right", {"start": v(-5.05, -20.65) * mm, "end": v(-5.05, -19.75) * mm});
            skSolve(sketch);
        }
        {
            var Q0;
            Q0=qSketchRegion(id+"F4",true);
            extrude(context, id + "F5", {"entities" : qUnion([Q0]), "operationType" : NewBodyOperationType.REMOVE, "endBound" : BoundingType.THROUGH_ALL, "oppositeDirection" : true, "depth" : 25.4 * mm});
        }
        {
            var Q0;
            Q0=makeQuery(id+"F1.opExtrude","CAP_FACE",FACE,{"disambiguationData":[OSD([sQuery(id+"F0.wireOp",EDGE,"E254"),sQuery(id+"F0.wireOp",EDGE,"E255"),sQuery(id+"F0.wireOp",EDGE,"E256"),sQuery(id+"F0.wireOp",EDGE,"E257"),sQuery(id+"F0.wireOp",EDGE,"E258"),sQuery(id+"F0.wireOp",EDGE,"E259"),sQuery(id+"F0.wireOp",EDGE,"E260"),sQuery(id+"F0.wireOp",EDGE,"E261"),sQuery(id+"F0.wireOp",EDGE,"E262"),sQuery(id+"F0.wireOp",EDGE,"E263"),sQuery(id+"F0.wireOp",EDGE,"E264"),sQuery(id+"F0.wireOp",EDGE,"E265"),sQuery(id+"F0.wireOp",EDGE,"E266"),sQuery(id+"F0.wireOp",EDGE,"E267"),sQuery(id+"F0.wireOp",EDGE,"E268"),sQuery(id+"F0.wireOp",EDGE,"E269")])],"isStart":false});
            var sketch = newSketch(context, id + "F6", { "sketchPlane" : qUnion([Q0])});
            skLineSegment(sketch, "E272.0", {"start": v(-7.74, 13.2) * mm, "end": v(-7.74, -3.49) * mm});
            skArc(sketch, "E272.1", {"start": v(-6.29, 20.62) * mm, "mid": v(-7.37, 16.98) * mm, "end": v(-7.74, 13.2) * mm});
            skLineSegment(sketch, "E272.2", {"start": v(20.99, -4.92) * mm, "end": v(20.99, -4.8) * mm});
            skArc(sketch, "E272.3", {"start": v(20.3, -5.95) * mm, "mid": v(20.8, -5.54) * mm, "end": v(20.99, -4.92) * mm});
            skArc(sketch, "E272.4", {"start": v(12.86, -7.4) * mm, "mid": v(16.65, -7.04) * mm, "end": v(20.3, -5.95) * mm});
            skLineSegment(sketch, "E272.5", {"start": v(-3.82, -7.4) * mm, "end": v(12.86, -7.4) * mm});
            skArc(sketch, "E272.6", {"start": v(20.99, -4.8) * mm, "mid": v(20.92, -4.4) * mm, "end": v(20.7, -4.06) * mm});
            skLineSegment(sketch, "E272.7", {"start": v(20.7, -4.06) * mm, "end": v(-4.39, -4.06) * mm});
            skLineSegment(sketch, "E272.8", {"start": v(-4.39, -4.06) * mm, "end": v(-4.39, 21.04) * mm});
            skArc(sketch, "E272.9", {"start": v(-4.39, 21.04) * mm, "mid": v(-4.73, 21.25) * mm, "end": v(-5.12, 21.32) * mm});
            skLineSegment(sketch, "E272.10", {"start": v(-5.12, 21.32) * mm, "end": v(-5.25, 21.32) * mm});
            skArc(sketch, "E272.11", {"start": v(-5.25, 21.32) * mm, "mid": v(-5.87, 21.13) * mm, "end": v(-6.29, 20.62) * mm});
            skArc(sketch, "E273.0", {"start": v(-7.74, -3.49) * mm, "mid": v(-6.6, -6.26) * mm, "end": v(-3.82, -7.4) * mm});
            skSolve(sketch);
        }
        {
            var Q0;
            Q0=qSketchRegion(id+"F6",true);
            extrude(context, id + "F7", {"entities" : qUnion([Q0]), "oppositeDirection" : true, "offsetDistance" : 25.4 * mm, "depth" : 5.16 * mm, "hasSecondDirection" : true, "secondDirectionOppositeDirection" : false, "secondDirectionDepth" : 1.98 * mm});
        }
        {
            var Q0;
            Q0=makeQuery(id+"F7.opExtrude","CAP_EDGE",EDGE,{"disambiguationData":[OSD([sQuery(id+"F6.wireOp",EDGE,"E272.4")])],"isStart":true});
            var Q1;
            Q1=makeQuery(id+"F7.opExtrude","CAP_EDGE",EDGE,{"disambiguationData":[OSD([sQuery(id+"F6.wireOp",EDGE,"E272.3")])],"isStart":true});
            var Q2;
            Q2=makeQuery(id+"F7.opExtrude","CAP_EDGE",EDGE,{"disambiguationData":[OSD([sQuery(id+"F6.wireOp",EDGE,"E272.2")])],"isStart":true});
            fillet(context, id + "F8", {"entities" : qUnion([Q0, Q1, Q2]), "radius" : 1.98 * mm, "tangentPropagation" : true, "allowEdgeOverflow" : false});
        }
        {
            var Q0;
            Q0=makeQuery(id+"F7.opExtrude","CAP_EDGE",EDGE,{"disambiguationData":[OSD([sQuery(id+"F6.wireOp",EDGE,"E272.4")])],"isStart":false});
            fillet(context, id + "F9", {"entities" : qUnion([Q0]), "radius" : 0.56 * mm, "tangentPropagation" : true, "allowEdgeOverflow" : false});
        }
        {
            var Q0;
            Q0=makeQuery(id+"F1.opExtrude","SWEPT_BODY",BODY,{"disambiguationData":[OSD([sQuery(id+"F0.wireOp",EDGE,"E254"),sQuery(id+"F0.wireOp",EDGE,"E255"),sQuery(id+"F0.wireOp",EDGE,"E256"),sQuery(id+"F0.wireOp",EDGE,"E257"),sQuery(id+"F0.wireOp",EDGE,"E258"),sQuery(id+"F0.wireOp",EDGE,"E259"),sQuery(id+"F0.wireOp",EDGE,"E260"),sQuery(id+"F0.wireOp",EDGE,"E261"),sQuery(id+"F0.wireOp",EDGE,"E262"),sQuery(id+"F0.wireOp",EDGE,"E263"),sQuery(id+"F0.wireOp",EDGE,"E264"),sQuery(id+"F0.wireOp",EDGE,"E265"),sQuery(id+"F0.wireOp",EDGE,"E266"),sQuery(id+"F0.wireOp",EDGE,"E267"),sQuery(id+"F0.wireOp",EDGE,"E268"),sQuery(id+"F0.wireOp",EDGE,"E269")])]});
            var Q1;
            Q1=makeQuery(id+"F7.opExtrude","SWEPT_BODY",BODY,{"disambiguationData":[OSD([sQuery(id+"F6.wireOp",EDGE,"E272.0"),sQuery(id+"F6.wireOp",EDGE,"E272.1"),sQuery(id+"F6.wireOp",EDGE,"E272.2"),sQuery(id+"F6.wireOp",EDGE,"E272.3"),sQuery(id+"F6.wireOp",EDGE,"E272.4"),sQuery(id+"F6.wireOp",EDGE,"E272.5"),sQuery(id+"F6.wireOp",EDGE,"E272.6"),sQuery(id+"F6.wireOp",EDGE,"E272.7"),sQuery(id+"F6.wireOp",EDGE,"E272.8"),sQuery(id+"F6.wireOp",EDGE,"E272.9"),sQuery(id+"F6.wireOp",EDGE,"E272.10"),sQuery(id+"F6.wireOp",EDGE,"E272.11"),sQuery(id+"F6.wireOp",EDGE,"E273.0")])]});
            booleanBodies(context, id + "F10", {"operationType" : BooleanOperationType.SUBTRACTION, "tools" : qUnion([Q0]), "targets" : qUnion([Q1]), "offset" : true, "offsetAll" : true, "offsetDistance" : 0.08 * mm, "keepTools" : true});
        }
        {
            var Q0;
            Q0=makeQuery(id+"F8.opFillet","BLEND_EDGE",EDGE,{"blendedFrom":[makeQuery(id+"F7.opExtrude","CAP_EDGE",EDGE,{"disambiguationData":[OSD([sQuery(id+"F6.wireOp",EDGE,"E272.1")])],"isStart":true}),makeQuery(id+"F7.opExtrude","SWEPT_FACE",FACE,{"disambiguationData":[OSD([sQuery(id+"F6.wireOp",EDGE,"E272.9")])]})],"blendedInto":[makeQuery(id+"F7.opExtrude","SWEPT_FACE",FACE,{"disambiguationData":[OSD([sQuery(id+"F6.wireOp",EDGE,"E272.9")])]})]});
            var Q1;
            Q1=makeQuery(id+"F8.opFillet","BLEND_EDGE",EDGE,{"blendedFrom":[makeQuery(id+"F7.opExtrude","CAP_EDGE",EDGE,{"disambiguationData":[OSD([sQuery(id+"F6.wireOp",EDGE,"E272.1")])],"isStart":true}),makeQuery(id+"F7.opExtrude","SWEPT_FACE",FACE,{"disambiguationData":[OSD([sQuery(id+"F6.wireOp",EDGE,"E272.10")])]})],"blendedInto":[makeQuery(id+"F7.opExtrude","SWEPT_FACE",FACE,{"disambiguationData":[OSD([sQuery(id+"F6.wireOp",EDGE,"E272.10")])]})]});
            var Q2;
            Q2=makeQuery(id+"F8.opFillet","BLEND_EDGE",EDGE,{"blendedFrom":[makeQuery(id+"F7.opExtrude","CAP_EDGE",EDGE,{"disambiguationData":[OSD([sQuery(id+"F6.wireOp",EDGE,"E272.1")])],"isStart":true}),makeQuery(id+"F7.opExtrude","SWEPT_FACE",FACE,{"disambiguationData":[OSD([sQuery(id+"F6.wireOp",EDGE,"E272.11")])]})],"blendedInto":[makeQuery(id+"F7.opExtrude","SWEPT_FACE",FACE,{"disambiguationData":[OSD([sQuery(id+"F6.wireOp",EDGE,"E272.11")])]})]});
            fillet(context, id + "F11", {"entities" : qUnion([Q0, Q1, Q2]), "radius" : 1.27 * mm, "tangentPropagation" : true, "allowEdgeOverflow" : false});
        }
        {
            var Q0;
            Q0=makeQuery(id+"F8.opFillet","BLEND_EDGE",EDGE,{"blendedFrom":[makeQuery(id+"F7.opExtrude","CAP_EDGE",EDGE,{"disambiguationData":[OSD([sQuery(id+"F6.wireOp",EDGE,"E272.4")])],"isStart":true}),makeQuery(id+"F7.opExtrude","SWEPT_FACE",FACE,{"disambiguationData":[OSD([sQuery(id+"F6.wireOp",EDGE,"E272.6")])]})],"blendedInto":[makeQuery(id+"F7.opExtrude","SWEPT_FACE",FACE,{"disambiguationData":[OSD([sQuery(id+"F6.wireOp",EDGE,"E272.6")])]})]});
            var Q1;
            Q1=makeQuery(id+"F8.opFillet","BLEND_EDGE",EDGE,{"blendedFrom":[makeQuery(id+"F7.opExtrude","CAP_EDGE",EDGE,{"disambiguationData":[OSD([sQuery(id+"F6.wireOp",EDGE,"E272.4")])],"isStart":true}),makeQuery(id+"F7.opExtrude","SWEPT_FACE",FACE,{"disambiguationData":[OSD([sQuery(id+"F6.wireOp",EDGE,"E272.2")])]})],"blendedInto":[makeQuery(id+"F7.opExtrude","SWEPT_FACE",FACE,{"disambiguationData":[OSD([sQuery(id+"F6.wireOp",EDGE,"E272.2")])]})]});
            var Q2;
            Q2=makeQuery(id+"F8.opFillet","BLEND_EDGE",EDGE,{"blendedFrom":[makeQuery(id+"F7.opExtrude","CAP_EDGE",EDGE,{"disambiguationData":[OSD([sQuery(id+"F6.wireOp",EDGE,"E272.4")])],"isStart":true}),makeQuery(id+"F7.opExtrude","SWEPT_FACE",FACE,{"disambiguationData":[OSD([sQuery(id+"F6.wireOp",EDGE,"E272.3")])]})],"blendedInto":[makeQuery(id+"F7.opExtrude","SWEPT_FACE",FACE,{"disambiguationData":[OSD([sQuery(id+"F6.wireOp",EDGE,"E272.3")])]})]});
            fillet(context, id + "F12", {"entities" : qUnion([Q0, Q1, Q2]), "radius" : 1.27 * mm, "tangentPropagation" : true, "allowEdgeOverflow" : false});
        }
    });
